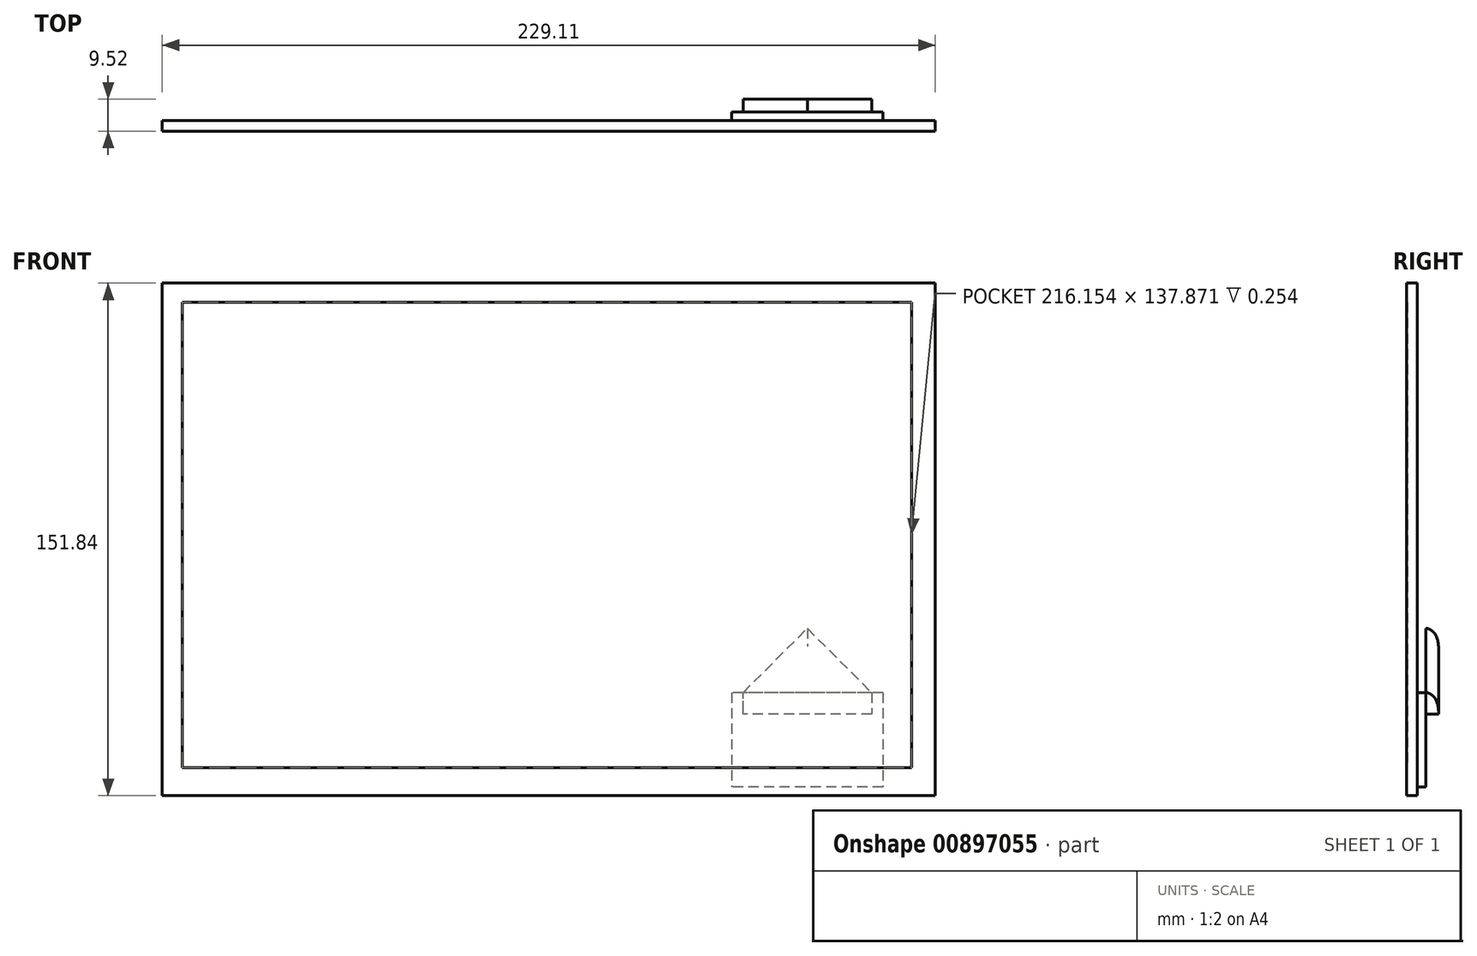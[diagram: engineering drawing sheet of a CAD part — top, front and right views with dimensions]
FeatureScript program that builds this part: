
annotation { "Feature Type Name" : "Feature", "Feature Type Description" : "" }
export const myFeature = defineFeature(function(context is Context, id is Id, definition is map)
    precondition{}
    {
        {
            var Q0;
            Q0=qCreatedBy(makeId("Front.planeOp"),FACE);
            var sketch = newSketch(context, id + "F0", { "sketchPlane" : qUnion([Q0])});
            skLineSegment(sketch, "E0.bottom", {"start": v(0, 0) * mm, "end": v(229.1, 0) * mm});
            skLineSegment(sketch, "E0.top", {"start": v(0, 151.84) * mm, "end": v(229.1, 151.84) * mm});
            skLineSegment(sketch, "E0.left", {"start": v(0, 0) * mm, "end": v(0, 151.84) * mm});
            skLineSegment(sketch, "E0.right", {"start": v(229.1, 0) * mm, "end": v(229.1, 151.84) * mm});
            skSolve(sketch);
        }
        {
            var Q0;
            Q0 = qSketchRegion(id + "F0", true);
            extrude(context, id + "F1", {"entities" : qUnion([Q0]), "depth" : 3.17 * mm, "offsetDistance" : 25.4 * mm});
        }
        {
            var Q0;
            Q0=makeQuery(id+"F1.opExtrude","CAP_FACE",FACE,{"disambiguationData":[OSD([sQuery(id+"F0.wireOp",EDGE,"E0.bottom"),sQuery(id+"F0.wireOp",EDGE,"E0.top"),sQuery(id+"F0.wireOp",EDGE,"E0.left"),sQuery(id+"F0.wireOp",EDGE,"E0.right")])],"isStart":false});
            var sketch = newSketch(context, id + "F2", { "sketchPlane" : qUnion([Q0])});
            skLineSegment(sketch, "E1.bottom", {"start": v(5.97, 146.13) * mm, "end": v(222.12, 146.13) * mm});
            skLineSegment(sketch, "E1.top", {"start": v(5.97, 8.26) * mm, "end": v(222.12, 8.26) * mm});
            skLineSegment(sketch, "E1.left", {"start": v(5.97, 146.13) * mm, "end": v(5.97, 8.25) * mm});
            skLineSegment(sketch, "E1.right", {"start": v(222.12, 146.13) * mm, "end": v(222.12, 8.25) * mm});
            skSolve(sketch);
        }
        {
            var Q0;
            Q0 = qSketchRegion(id + "F2", true);
            extrude(context, id + "F3", {"entities" : qUnion([Q0]), "operationType" : NewBodyOperationType.REMOVE, "oppositeDirection" : true, "depth" : 0.25 * mm, "offsetDistance" : 25.4 * mm});
        }
        {
            var Q0;
            Q0=makeQuery(id+"F1.opExtrude","CAP_FACE",FACE,{"disambiguationData":[OSD([sQuery(id+"F0.wireOp",EDGE,"E0.bottom"),sQuery(id+"F0.wireOp",EDGE,"E0.top"),sQuery(id+"F0.wireOp",EDGE,"E0.left"),sQuery(id+"F0.wireOp",EDGE,"E0.right")])],"isStart":true});
            var sketch = newSketch(context, id + "F4", { "sketchPlane" : qUnion([Q0])});
            skLineSegment(sketch, "E2.bottom", {"start": v(-213.55, 30.48) * mm, "end": v(-168.78, 30.48) * mm});
            skLineSegment(sketch, "E2.top", {"start": v(-213.55, 2.54) * mm, "end": v(-168.78, 2.54) * mm});
            skLineSegment(sketch, "E2.left", {"start": v(-213.55, 30.48) * mm, "end": v(-213.55, 2.54) * mm});
            skLineSegment(sketch, "E2.right", {"start": v(-168.78, 30.48) * mm, "end": v(-168.78, 2.54) * mm});
            skSolve(sketch);
        }
        {
            var Q0;
            Q0 = qSketchRegion(id + "F4", true);
            extrude(context, id + "F5", {"entities" : qUnion([Q0]), "operationType" : NewBodyOperationType.ADD, "depth" : 2.54 * mm, "offsetDistance" : 25.4 * mm});
        }
        {
            var Q0;
            Q0=makeQuery(id+"F5.opExtrude","CAP_FACE",FACE,{"disambiguationData":[OSD([sQuery(id+"F4.wireOp",EDGE,"E2.bottom"),sQuery(id+"F4.wireOp",EDGE,"E2.top"),sQuery(id+"F4.wireOp",EDGE,"E2.left"),sQuery(id+"F4.wireOp",EDGE,"E2.right")])],"isStart":false});
            var sketch = newSketch(context, id + "F6", { "sketchPlane" : qUnion([Q0])});
            skLineSegment(sketch, "E3", {"start": v(-210.22, 24.13) * mm, "end": v(-172.12, 24.13) * mm});
            skLineSegment(sketch, "E4", {"start": v(-172.12, 24.13) * mm, "end": v(-172.12, 30.48) * mm});
            skLineSegment(sketch, "E5", {"start": v(-172.12, 30.48) * mm, "end": v(-191.17, 49.53) * mm});
            skLineSegment(sketch, "E6", {"start": v(-191.17, 49.53) * mm, "end": v(-210.22, 30.48) * mm});
            skLineSegment(sketch, "E7", {"start": v(-210.22, 30.48) * mm, "end": v(-210.22, 24.13) * mm});
            skPoint(sketch, "E8", {"position": v(-191.17, 24.13) * mm});
            skPoint(sketch, "E9", {"position": v(-191.17, 30.48) * mm});
            skSolve(sketch);
        }
        {
            var Q0;
            Q0 = qSketchRegion(id + "F6", true);
            extrude(context, id + "F7", {"entities" : qUnion([Q0]), "operationType" : NewBodyOperationType.ADD, "depth" : 3.8 * mm, "offsetDistance" : 25.4 * mm});
        }
        {
            var Q0;
            Q0=makeQuery(id+"F7.opExtrude","CAP_EDGE",EDGE,{"disambiguationData":[OSD([sQuery(id+"F6.wireOp",EDGE,"E6")])],"isStart":false});
            var Q1;
            Q1=makeQuery(id+"F7.opExtrude","CAP_EDGE",EDGE,{"disambiguationData":[OSD([sQuery(id+"F6.wireOp",EDGE,"E5")])],"isStart":false});
            fillet(context, id + "F8", {"entities" : qUnion([Q0, Q1]), "radius" : 3.8 * mm, "tangentPropagation" : true, "allowEdgeOverflow" : false});
        }
    });
